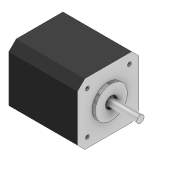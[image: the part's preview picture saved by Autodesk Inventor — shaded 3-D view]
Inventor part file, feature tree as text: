
AUTODESK INVENTOR PART (.ipt)
format: ipt  version: 2020 (Build 240168000, 168)  size: 152,576 bytes
history: native  units: in
note: dims shown in document units (in); Inventor stores cm internally (conversion verified against a paired STEP export)
features: extrude x4, sketch x4, chamfer x1
ambient origin geometry x8: Origin, YZ Plane, XZ Plane, XY Plane, X Axis, Y Axis, Z Axis, Center Point
bodies: Solid1 (feature_tree)
feature tree (9):
  extrude  "Extrusion1"  Depth=1.6535in
  extrude  "Extrusion2"  Depth=0.8661in
  extrude  "Extrusion3"  Depth=0.0787in TaperAngle=0.0deg
  chamfer  "Chamfer1"  Distance=0.8661in
  extrude  "Extrusion4"  Depth=0.1969in TaperAngle=45.0deg
  sketch  "Sketch1"  dims[d0=1.6535in d1=1.6535in]
  sketch  "Sketch2"  dims[d2=1.8504in d3=0.0in d4=0.8661in]
  sketch  "Sketch3"  dims[d5=0.315in d6=0.0787in d7=0.0in]
  sketch  "Sketch4"  dims[d8=0.1969in d9=0.8661in d10=0.0in d11=0.1969in d12=0.125in d13=45.0deg d14=1.1319in d15=1.1319in d16=0.2608in d17=0.2608in d18=0.0984in d19=0.0984in d20=0.0984in d21=0.0984in d22=0.1969in d23=0.0in]
